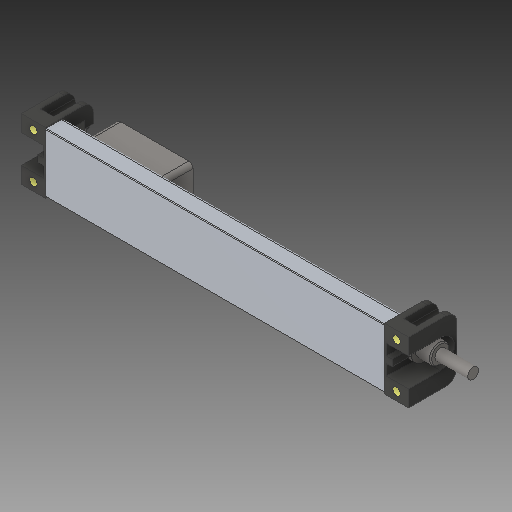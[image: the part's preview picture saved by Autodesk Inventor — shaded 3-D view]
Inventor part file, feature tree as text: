
AUTODESK INVENTOR PART (.ipt)
format: ipt  version: 2019 (Build 230136000, 136)  size: 556,544 bytes
history: native  units: mm
features: other x4, sketch x1
ambient origin geometry x8: Origin, YZ Plane, XZ Plane, XY Plane, X Axis, Y Axis, Z Axis, Center Point
bodies: Solid1 (feature_tree), Solid2 (feature_tree)
feature tree (5):
  other  "SLNV_27_100_2.ipt"
  other  "Solid1::SLNV_27_100_2.ipt"
  other  "Solid2::SLNV_27_100_2.ipt"
  other  "TaggingFeature1"
  sketch  "Sketch1"  dims[d0=10.0mm]
